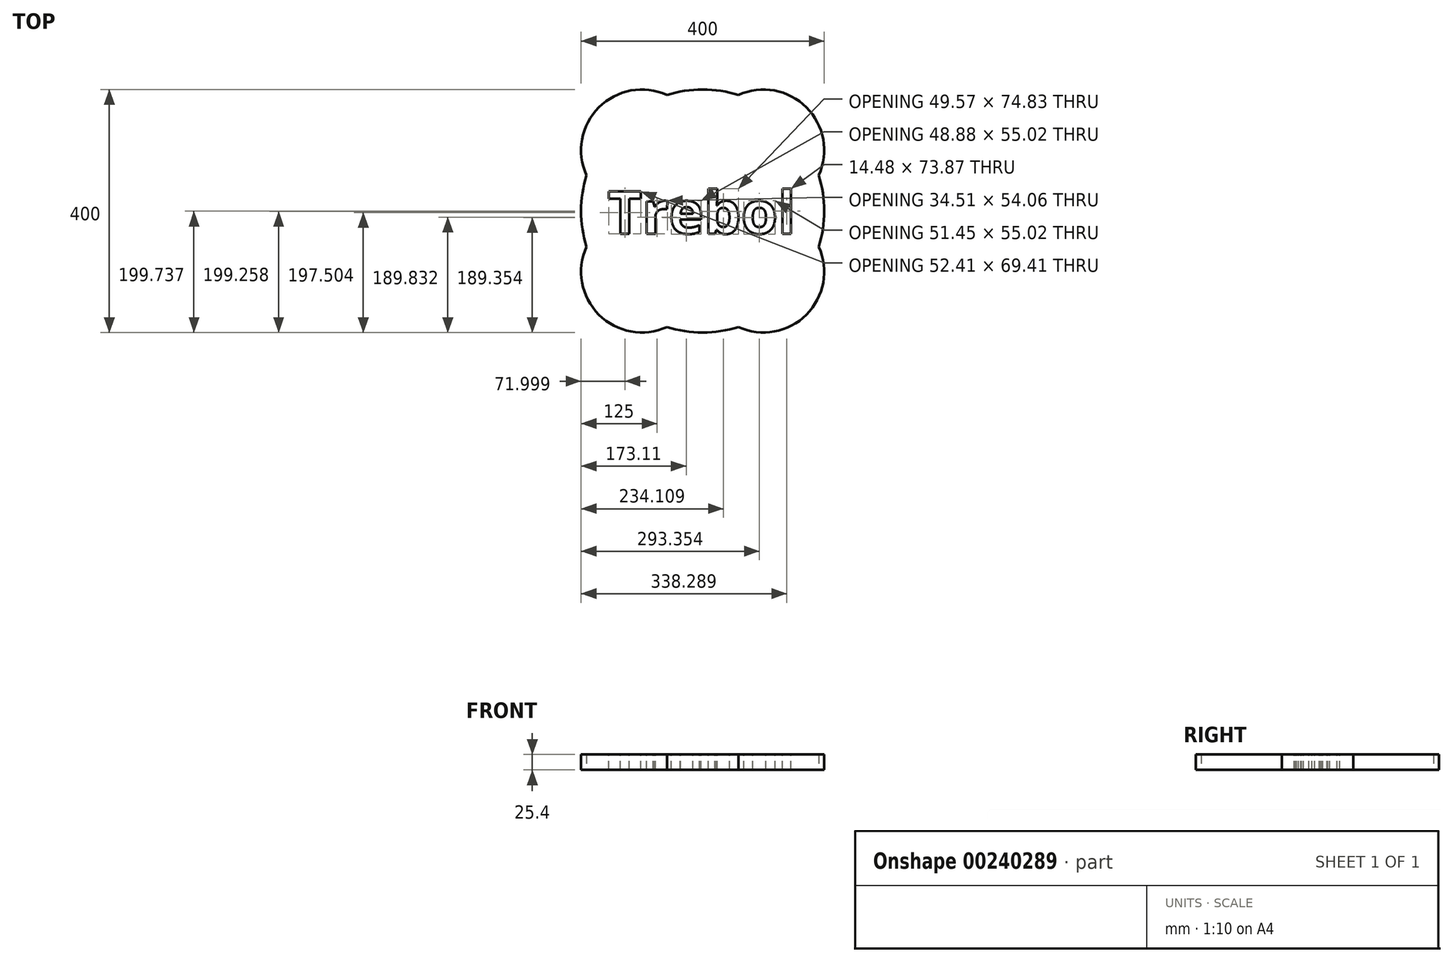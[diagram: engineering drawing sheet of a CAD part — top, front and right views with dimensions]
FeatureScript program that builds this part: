
annotation { "Feature Type Name" : "Feature", "Feature Type Description" : "" }
export const myFeature = defineFeature(function(context is Context, id is Id, definition is map)
    precondition{}
    {
        {
            var Q0;
            Q0=qCreatedBy(makeId("Top.planeOp"),FACE);
            var sketch = newSketch(context, id + "F0", { "sketchPlane" : qUnion([Q0])});
            skLineSegment(sketch, "E0.bottom", {"start": v(-100, 100) * mm, "end": v(100, 100) * mm, "construction": true});
            skLineSegment(sketch, "E0.top", {"start": v(-100, -100) * mm, "end": v(100, -100) * mm, "construction": true});
            skLineSegment(sketch, "E0.left", {"start": v(-100, 100) * mm, "end": v(-100, -100) * mm, "construction": true});
            skLineSegment(sketch, "E0.right", {"start": v(100, 100) * mm, "end": v(100, -100) * mm, "construction": true});
            skPoint(sketch, "E0.middle", {"position": v(0, 0) * mm});
            skArc(sketch, "E1", {"start": v(-191.14, 58.86) * mm, "mid": v(-200, 0) * mm, "end": v(-191.14, -58.86) * mm});
            skArc(sketch, "E2", {"start": v(191.14, 58.86) * mm, "mid": v(170.71, 170.71) * mm, "end": v(58.86, 191.14) * mm});
            skArc(sketch, "E3", {"start": v(-58.86, 191.14) * mm, "mid": v(-170.71, 170.71) * mm, "end": v(-191.14, 58.86) * mm});
            skArc(sketch, "E4", {"start": v(-191.14, -58.86) * mm, "mid": v(-170.71, -170.71) * mm, "end": v(-58.86, -191.14) * mm});
            skArc(sketch, "E5", {"start": v(58.86, -191.14) * mm, "mid": v(170.71, -170.71) * mm, "end": v(191.14, -58.86) * mm});
            skArc(sketch, "E6.trimOffspring", {"start": v(-58.86, -191.14) * mm, "mid": v(0, -200) * mm, "end": v(58.86, -191.14) * mm});
            skArc(sketch, "E7.trimOffspring", {"start": v(191.14, -58.86) * mm, "mid": v(200, 0) * mm, "end": v(191.14, 58.86) * mm});
            skArc(sketch, "E8.trimOffspring", {"start": v(58.86, 191.14) * mm, "mid": v(0, 200) * mm, "end": v(-58.86, 191.14) * mm});
            skSolve(sketch);
        }
        {
            var Q0;
            Q0 = qSketchRegion(id + "F0", true);
            extrude(context, id + "F1", {"entities" : qUnion([Q0]), "depth" : 25.4 * mm});
        }
        {
            var Q0;
            Q0=makeQuery(id+"F1.opExtrude","CAP_FACE",FACE,{"disambiguationData":[OSD([sQuery(id+"F0.wireOp",EDGE,"E1"),sQuery(id+"F0.wireOp",EDGE,"E2"),sQuery(id+"F0.wireOp",EDGE,"E3"),sQuery(id+"F0.wireOp",EDGE,"E4"),sQuery(id+"F0.wireOp",EDGE,"E5"),sQuery(id+"F0.wireOp",EDGE,"E6.trimOffspring"),sQuery(id+"F0.wireOp",EDGE,"E7.trimOffspring"),sQuery(id+"F0.wireOp",EDGE,"E8.trimOffspring")])],"isStart":false});
            var sketch = newSketch(context, id + "F2", { "sketchPlane" : qUnion([Q0])});
            skText(sketch, "E9", { "text": "Trebol", "fontName": "OpenSans-Bold.ttf"});
            const initialGuessF2  = {"E9": [-0.15615, -0.0372, 1, 0, 0.07]};
            skSetInitialGuess(sketch, initialGuessF2);
            skSolve(sketch);
        }
        {
            var Q0;
            Q0 = qSketchRegion(id + "F2", true);
            extrude(context, id + "F3", {"entities" : qUnion([Q0]), "operationType" : NewBodyOperationType.REMOVE, "oppositeDirection" : true, "depth" : 25.4 * mm});
        }
    });
